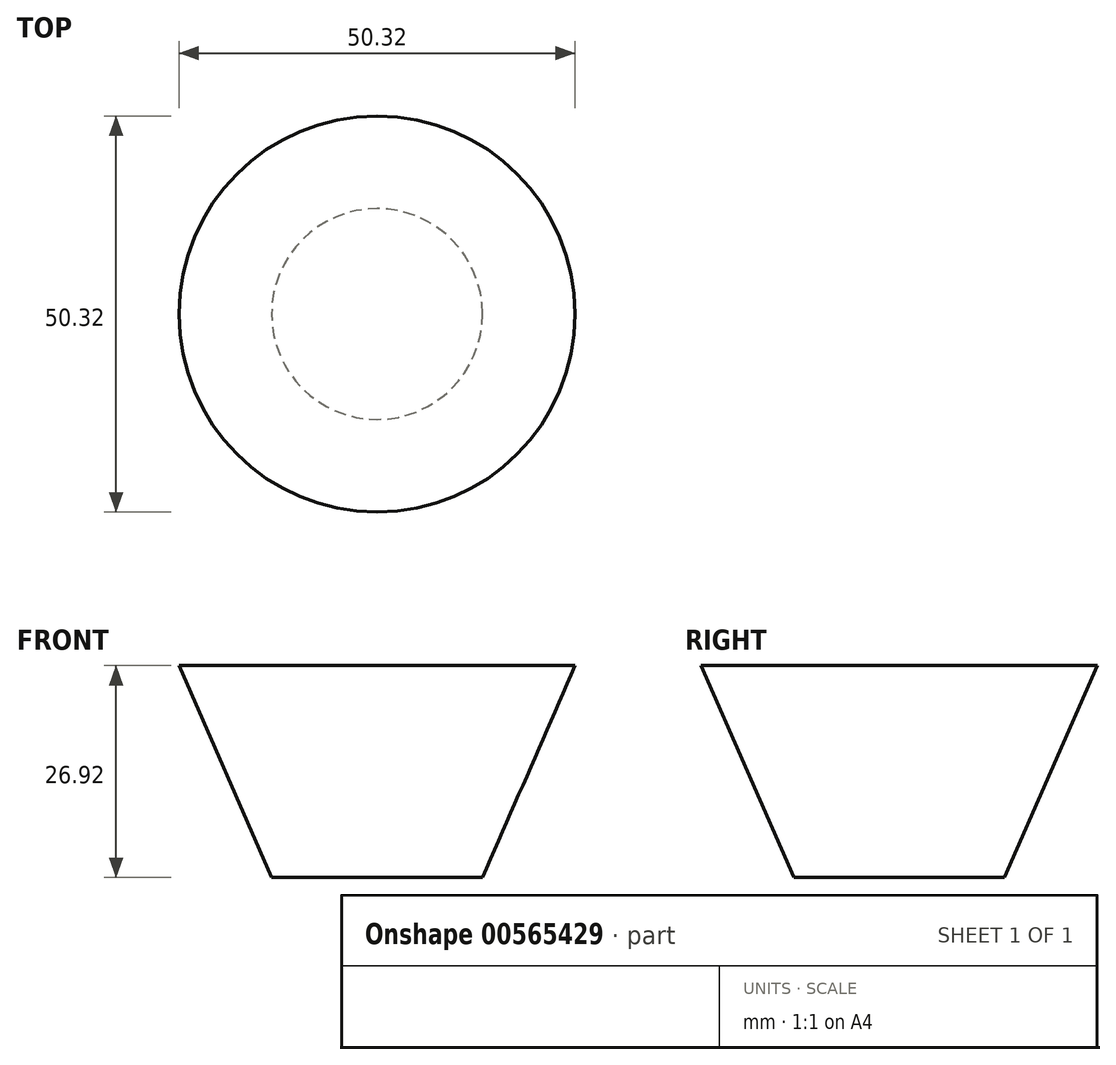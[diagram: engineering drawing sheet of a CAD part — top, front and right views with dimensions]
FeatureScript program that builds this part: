
annotation { "Feature Type Name" : "Feature", "Feature Type Description" : "" }
export const myFeature = defineFeature(function(context is Context, id is Id, definition is map)
    precondition{}
    {
        {
            var Q0;
            Q0=qCreatedBy(makeId("Top.planeOp"),FACE);
            var sketch = newSketch(context, id + "F0", { "sketchPlane" : qUnion([Q0])});
            skCircle(sketch, "E0", {"center": v(0, 0) * mm, "radius": 25.16 * mm});
            skSolve(sketch);
        }
        {
            var Q0;
            Q0=qCreatedBy(makeId("Top.planeOp"),FACE);
            cPlane(context, id + "F1", {"entities" : qUnion([Q0]), "cplaneType" : CPlaneType.OFFSET, "offset" : 26.92 * mm, "oppositeDirection" : true, "width" : 152.4 * mm, "height" : 152.4 * mm});
        }
        {
            var Q0;
            Q0=qCreatedBy(id+"F1.planeOp",FACE);
            var sketch = newSketch(context, id + "F2", { "sketchPlane" : qUnion([Q0])});
            skCircle(sketch, "E1", {"center": v(0, 0) * mm, "radius": 13.4 * mm});
            skSolve(sketch);
        }
        {
            var Q0;
            Q0=makeQuery(id+"F2.imprint","IMPRINT",FACE,{"disambiguationData":[TD([[makeQuery(id+"F2.imprint","IMPRINT",EDGE,{"derivedFrom":sQuery(id+"F2.wireOp",EDGE,"E1")}),1.0]])]});
            var Q1;
            Q1=makeQuery(id+"F0.imprint","IMPRINT",FACE,{"disambiguationData":[TD([[makeQuery(id+"F0.imprint","IMPRINT",EDGE,{"derivedFrom":sQuery(id+"F0.wireOp",EDGE,"E0")}),1.0]])]});
            loft(context, id + "F3", {"sheetProfilesArray" : [{ "sheetProfileEntities" : qUnion([Q0]) }, { "sheetProfileEntities" : qUnion([Q1]) }]});
        }
    });
